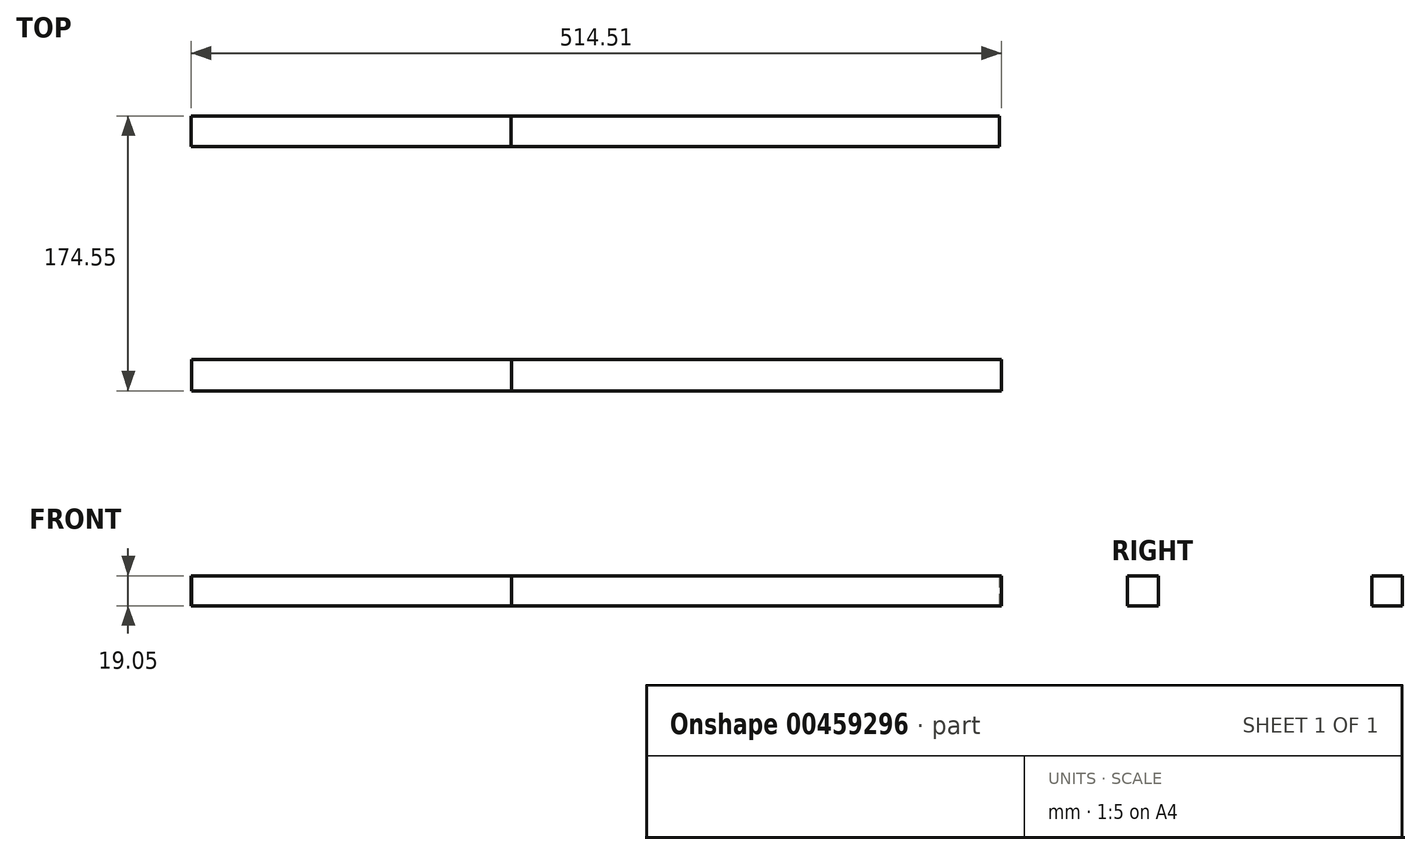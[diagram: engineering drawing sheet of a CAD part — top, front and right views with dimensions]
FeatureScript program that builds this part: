
annotation { "Feature Type Name" : "Feature", "Feature Type Description" : "" }
export const myFeature = defineFeature(function(context is Context, id is Id, definition is map)
    precondition{}
    {
        {
            var Q0;
            Q0=qCreatedBy(makeId("Top.planeOp"),FACE);
            var sketch = newSketch(context, id + "F0", { "sketchPlane" : qUnion([Q0])});
            skLineSegment(sketch, "E0.bottom", {"start": v(-155.43, -86.27) * mm, "end": v(155.74, -86.27) * mm});
            skLineSegment(sketch, "E0.top", {"start": v(-155.43, -66.44) * mm, "end": v(155.74, -66.44) * mm});
            skLineSegment(sketch, "E0.left", {"start": v(-155.43, -86.27) * mm, "end": v(-155.43, -66.44) * mm});
            skLineSegment(sketch, "E0.right", {"start": v(155.74, -86.27) * mm, "end": v(155.74, -66.44) * mm});
            skLineSegment(sketch, "E1.bottom", {"start": v(-155.57, 88.28) * mm, "end": v(154.5, 88.28) * mm});
            skLineSegment(sketch, "E1.top", {"start": v(-155.57, 69) * mm, "end": v(154.5, 69) * mm});
            skLineSegment(sketch, "E1.left", {"start": v(-155.57, 88.28) * mm, "end": v(-155.57, 69) * mm});
            skLineSegment(sketch, "E1.right", {"start": v(154.5, 88.28) * mm, "end": v(154.5, 69) * mm});
            skSolve(sketch);
        }
        {
            var Q0;
            Q0 = qSketchRegion(id + "F0", true);
            extrude(context, id + "F1", {"entities" : qUnion([Q0]), "depth" : 19.05 * mm});
        }
        {
            var Q0;
            Q0=makeQuery(id+"F1.opExtrude","SWEPT_FACE",FACE,{"disambiguationData":[OSD([sQuery(id+"F0.wireOp",EDGE,"E1.left")])]});
            var Q1;
            Q1=makeQuery(id+"F1.opExtrude","SWEPT_FACE",FACE,{"disambiguationData":[OSD([sQuery(id+"F0.wireOp",EDGE,"E0.left")])]});
            extrude(context, id + "F2", {"entities" : qUnion([Q0, Q1]), "depth" : 203.2 * mm});
        }
    });
